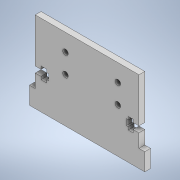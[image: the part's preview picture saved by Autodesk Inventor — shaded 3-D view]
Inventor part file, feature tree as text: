
AUTODESK INVENTOR PART (.ipt)
format: ipt  version: 2022 (Build 260153000, 153)  size: 173,056 bytes
history: native  units: mm
features: reference x4, other x2, extrude x1, sketch x1
ambient origin geometry x8: Origin, YZ Plane, XZ Plane, XY Plane, X Axis, Y Axis, Z Axis, Center Point
bodies: Solid1 (feature_tree)
feature tree (8):
  extrude  "Extrusion1"  Depth=9.0mm
  sketch  "Sketch1"  dims[d9=7.0mm d10=2.5mm d27=3.0mm d28=0.0mm d54=3.1mm d70=3.1mm d74=1.5mm d83=3.0mm d85=3.1mm d87=3.0mm d100=9.0mm d102=3.1mm d103=0.0mm d104=0.0mm d105=53.5mm d108=3.0mm d109=9.0mm d110=9.0mm d111=0.0mm d112=3.0mm d113=3.0mm d114=2.5mm d115=1.0mm d116=1.0mm d117=1.5mm d121=8.5mm d122=1.55mm d123=6.95mm d124=6.95mm d125=1.0mm d126=1.0mm d127=3.0mm d128=3.0mm d129=1.5mm d130=1.5mm d131=0.0mm d132=1.5mm d133=1.5mm d134=1.5mm d136=27.0mm]
  reference  "Reference5"
  reference  "Reference6"
  reference  "Reference7"
  reference  "Reference8"
  other  "EnsambleCuerpo.iam"
  other  "Muñeca2:1"
